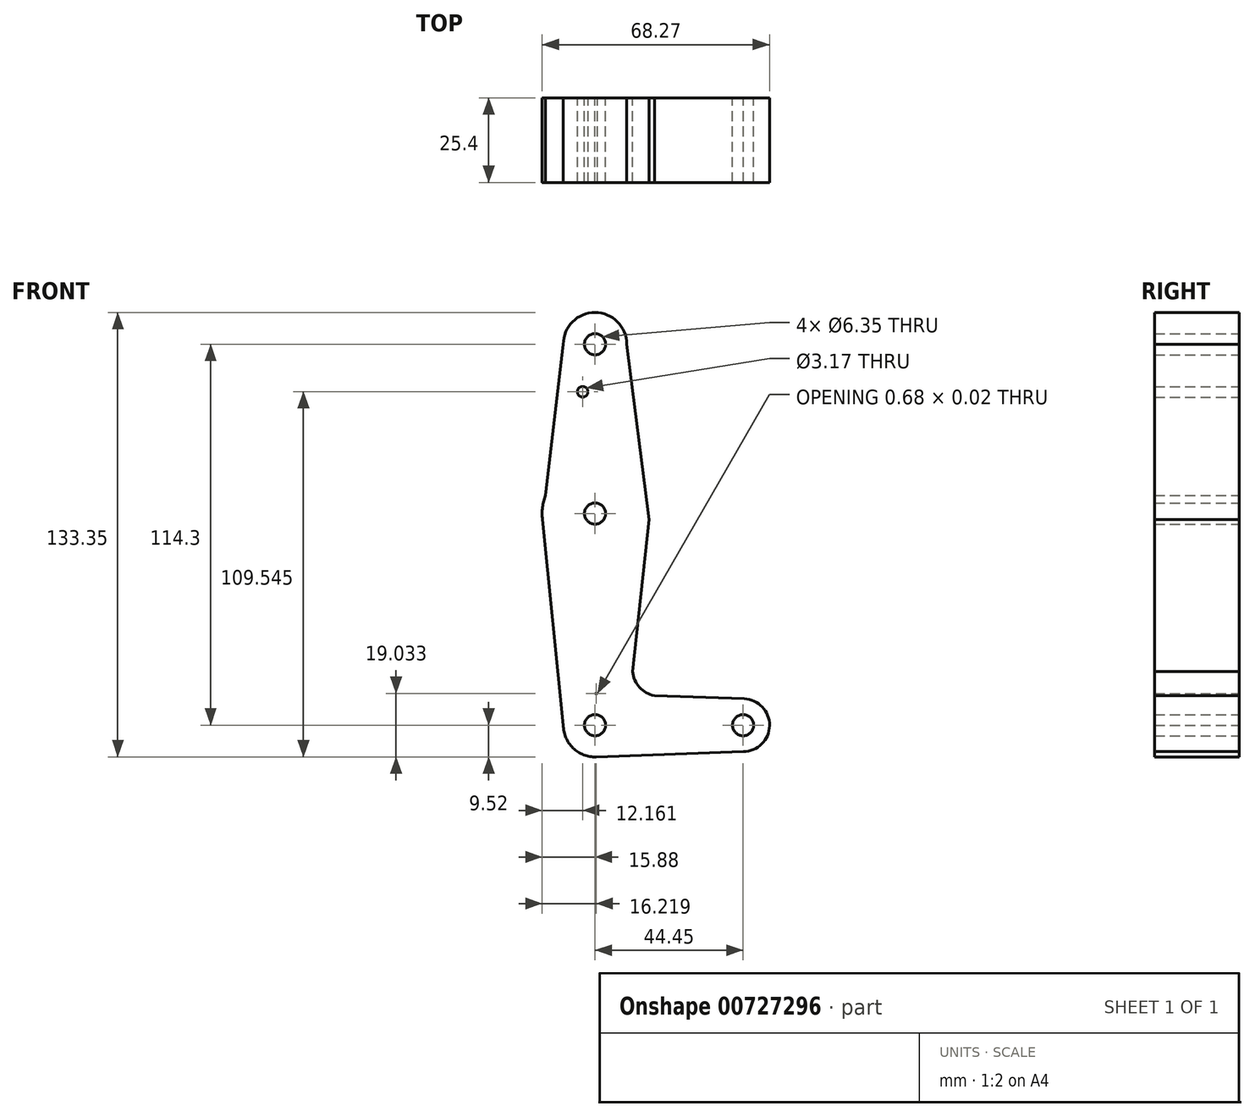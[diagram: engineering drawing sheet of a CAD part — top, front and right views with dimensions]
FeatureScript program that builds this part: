
annotation { "Feature Type Name" : "Feature", "Feature Type Description" : "" }
export const myFeature = defineFeature(function(context is Context, id is Id, definition is map)
    precondition{}
    {
        {
            var Q0;
            Q0=qCreatedBy(makeId("Front.planeOp"),FACE);
            var sketch = newSketch(context, id + "F0", { "sketchPlane" : qUnion([Q0])});
            skLineSegment(sketch, "E0", {"start": v(0, 0) * mm, "end": v(0, 114.3) * mm});
            skLineSegment(sketch, "E1", {"start": v(0, 114.3) * mm, "end": v(0, 0) * mm, "construction": true});
            skLineSegment(sketch, "E2", {"start": v(44.45, 0) * mm, "end": v(0, 0) * mm, "construction": true});
            skCircle(sketch, "E3", {"center": v(0, 0) * mm, "radius": 9.53 * mm});
            skCircle(sketch, "E4", {"center": v(44.45, 0) * mm, "radius": 7.94 * mm});
            skCircle(sketch, "E5", {"center": v(0, 114.3) * mm, "radius": 9.53 * mm});
            skCircle(sketch, "E6", {"center": v(0, 63.5) * mm, "radius": 15.88 * mm});
            skLineSegment(sketch, "E7", {"start": v(-9.53, 114.3) * mm, "end": v(-15.78, 61.72) * mm});
            skLineSegment(sketch, "E8", {"start": v(-9.53, 0) * mm, "end": v(-15.78, 61.72) * mm});
            skLineSegment(sketch, "E9", {"start": v(9.52, 114.3) * mm, "end": v(16.23, 61.72) * mm});
            skLineSegment(sketch, "E10", {"start": v(16.23, 61.72) * mm, "end": v(9.58, 0) * mm});
            skLineSegment(sketch, "E11", {"start": v(0, 9.53) * mm, "end": v(44.73, 7.93) * mm});
            skLineSegment(sketch, "E12", {"start": v(44.97, -7.92) * mm, "end": v(0, -9.53) * mm});
            skCircle(sketch, "E13", {"center": v(0, 114.3) * mm, "radius": 3.18 * mm});
            skCircle(sketch, "E14", {"center": v(0, 63.5) * mm, "radius": 3.18 * mm});
            skCircle(sketch, "E15", {"center": v(0, 0) * mm, "radius": 3.18 * mm});
            skCircle(sketch, "E16", {"center": v(44.45, 0) * mm, "radius": 3.18 * mm});
            skCircle(sketch, "E17", {"center": v(-3.72, 100.03) * mm, "radius": 1.59 * mm});
            skArc(sketch, "E18", {"start": v(11.63, 19) * mm, "mid": v(12.46, 12.56) * mm, "end": v(17.82, 8.9) * mm});
            skSolve(sketch);
        }
        {
            var Q0;
            Q0 = qSketchRegion(id + "F0", true);
            extrude(context, id + "F1", {"entities" : qUnion([Q0]), "depth" : 25.4 * mm, "offsetDistance" : 25.4 * mm});
        }
    });
